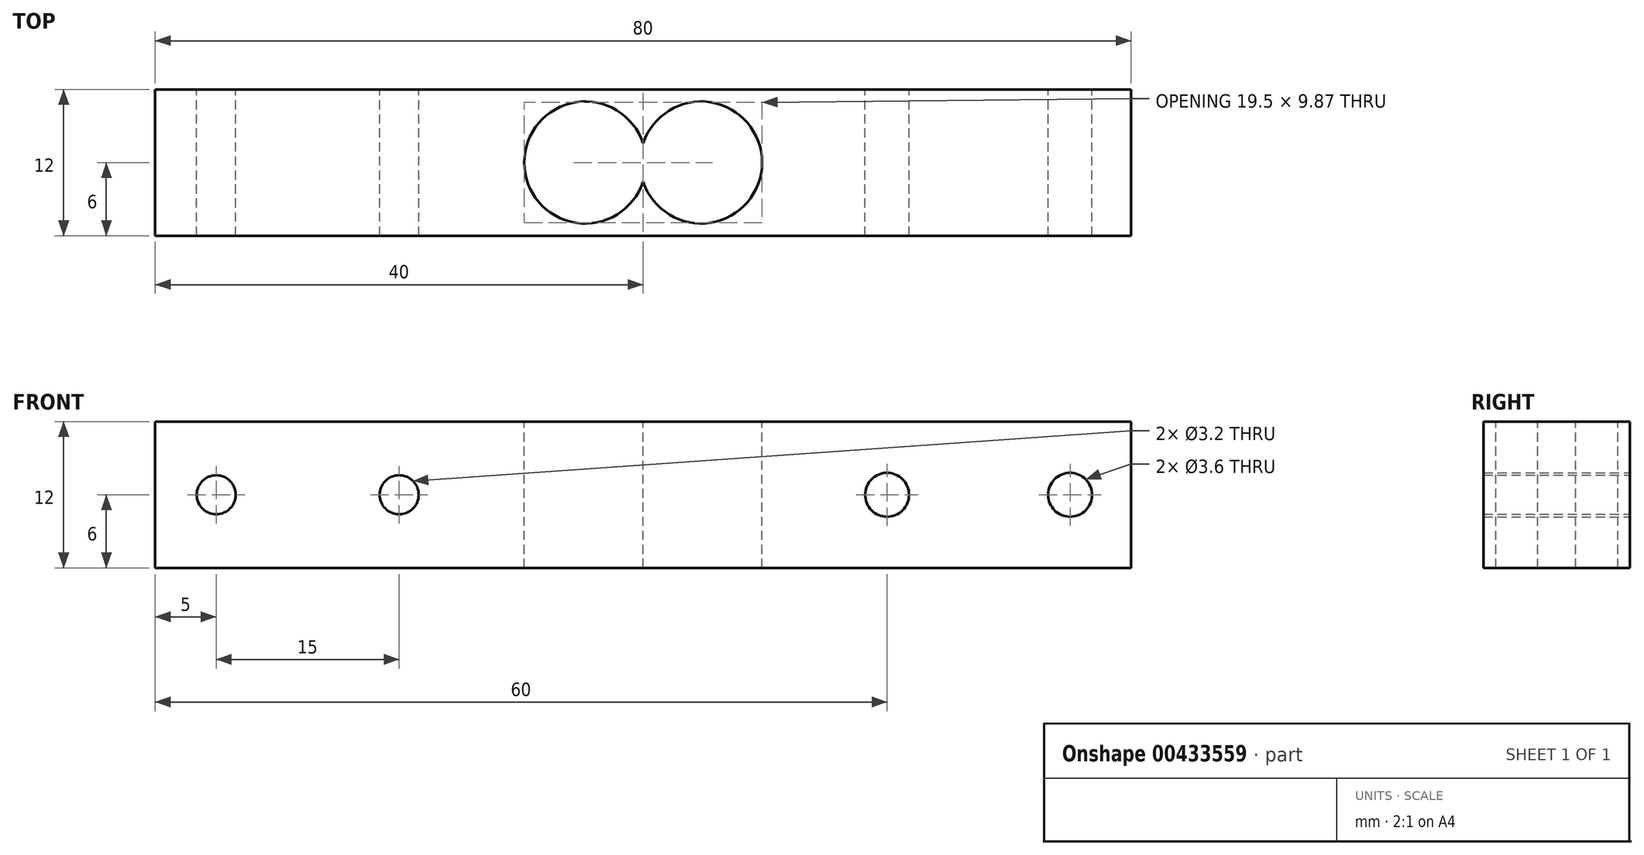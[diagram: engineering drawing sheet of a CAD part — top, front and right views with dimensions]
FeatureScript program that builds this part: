
annotation { "Feature Type Name" : "Feature", "Feature Type Description" : "" }
export const myFeature = defineFeature(function(context is Context, id is Id, definition is map)
    precondition{}
    {
        {
            var Q0;
            Q0=qCreatedBy(makeId("Front.planeOp"),FACE);
            var sketch = newSketch(context, id + "F0", { "sketchPlane" : qUnion([Q0])});
            skLineSegment(sketch, "E0.bottom", {"start": v(0, 0) * mm, "end": v(80, 0) * mm});
            skLineSegment(sketch, "E0.top", {"start": v(0, 12) * mm, "end": v(80, 12) * mm});
            skLineSegment(sketch, "E0.left", {"start": v(0, 0) * mm, "end": v(0, 12) * mm});
            skLineSegment(sketch, "E0.right", {"start": v(80, 0) * mm, "end": v(80, 12) * mm});
            skSolve(sketch);
        }
        {
            var Q0;
            Q0 = qSketchRegion(id + "F0", true);
            extrude(context, id + "F1", {"entities" : qUnion([Q0]), "depth" : 12 * mm});
        }
        {
            var Q0;
            Q0=makeQuery(id+"F1.opExtrude","SWEPT_FACE",FACE,{"disambiguationData":[OSD([sQuery(id+"F0.wireOp",EDGE,"E0.top")])]});
            var sketch = newSketch(context, id + "F2", { "sketchPlane" : qUnion([Q0])});
            skCircle(sketch, "E1", {"center": v(35.25, -6) * mm, "radius": 5 * mm});
            skSolve(sketch);
        }
        {
            var Q0;
            Q0=makeQuery(id+"F2.imprint","IMPRINT",FACE,{"disambiguationData":[TD([[makeQuery(id+"F2.imprint","IMPRINT",EDGE,{"derivedFrom":sQuery(id+"F2.wireOp",EDGE,"E1")}),-1.0]])]});
            var sketch = newSketch(context, id + "F3", { "sketchPlane" : qUnion([Q0])});
            skCircle(sketch, "E2", {"center": v(44.75, -6) * mm, "radius": 5 * mm});
            skSolve(sketch);
        }
        {
            var Q0;
            Q0 = qSketchRegion(id + "F3", true);
            extrude(context, id + "F4", {"entities" : qUnion([Q0]), "operationType" : NewBodyOperationType.REMOVE, "oppositeDirection" : true, "depth" : 25 * mm});
        }
        {
            var Q0;
            Q0 = qSketchRegion(id + "F2", true);
            extrude(context, id + "F5", {"entities" : qUnion([Q0]), "operationType" : NewBodyOperationType.REMOVE, "oppositeDirection" : true, "depth" : 25 * mm});
        }
        {
            var Q0;
            Q0=makeQuery(id+"F1.opExtrude","CAP_FACE",FACE,{"disambiguationData":[OSD([sQuery(id+"F0.wireOp",EDGE,"E0.bottom"),sQuery(id+"F0.wireOp",EDGE,"E0.top"),sQuery(id+"F0.wireOp",EDGE,"E0.left"),sQuery(id+"F0.wireOp",EDGE,"E0.right")])],"isStart":true});
            var sketch = newSketch(context, id + "F6", { "sketchPlane" : qUnion([Q0])});
            skCircle(sketch, "E3", {"center": v(-5, 6) * mm, "radius": 1.6 * mm});
            skCircle(sketch, "E4", {"center": v(-20, 6) * mm, "radius": 1.6 * mm});
            skCircle(sketch, "E5", {"center": v(-75, 6) * mm, "radius": 1.8 * mm});
            skCircle(sketch, "E6", {"center": v(-60, 6) * mm, "radius": 1.8 * mm});
            skSolve(sketch);
        }
        {
            var Q0;
            Q0 = qSketchRegion(id + "F6", true);
            extrude(context, id + "F7", {"entities" : qUnion([Q0]), "operationType" : NewBodyOperationType.REMOVE, "oppositeDirection" : true, "depth" : 25 * mm});
        }
    });
